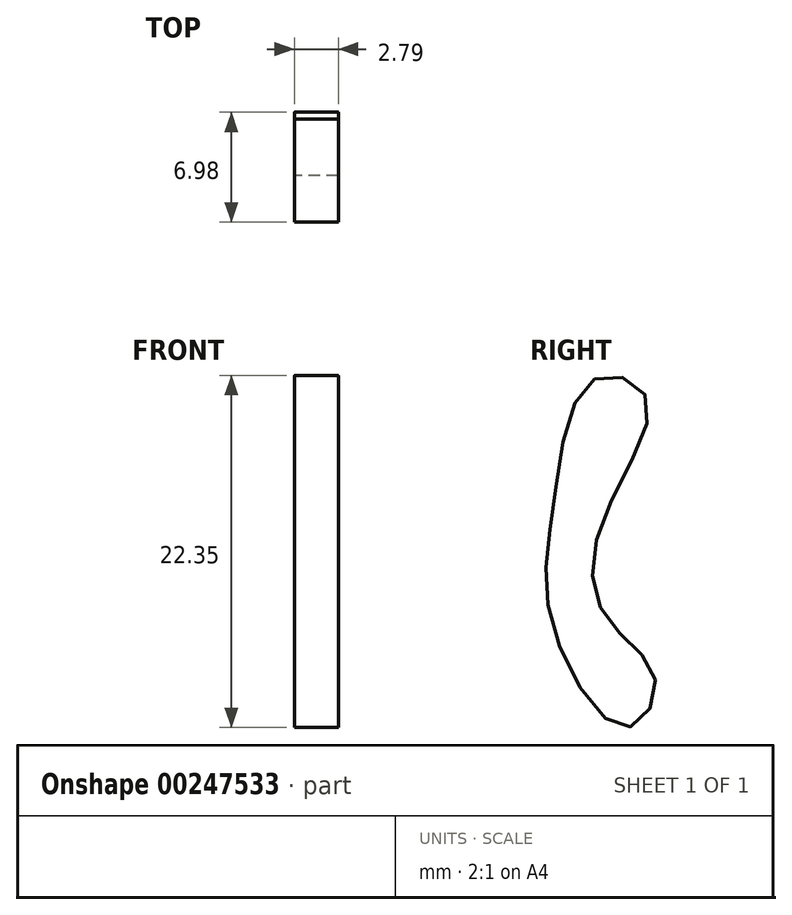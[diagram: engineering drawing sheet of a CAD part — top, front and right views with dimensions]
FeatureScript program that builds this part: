
annotation { "Feature Type Name" : "Feature", "Feature Type Description" : "" }
export const myFeature = defineFeature(function(context is Context, id is Id, definition is map)
    precondition{}
    {
        {
            var Q0;
            Q0=qCreatedBy(makeId("Right.planeOp"),FACE);
            var sketch = newSketch(context, id + "F0", { "sketchPlane" : qUnion([Q0])});
            skFitSpline(sketch, "E0", {"points": [v(-40.65, 39.62) * mm, v(-43.22, 31.9) * mm, v(-43.22, 23.67) * mm, v(-38.6, 17.5) * mm, v(-36.79, 20.58) * mm, v(-39.88, 24.44) * mm, v(-40.13, 30.61) * mm, v(-37.3, 38.33) * mm, v(-40.65, 39.62) * mm]});
            skSolve(sketch);
        }
        {
            var Q0;
            Q0 = qSketchRegion(id + "F0", true);
            extrude(context, id + "F1", {"entities" : qUnion([Q0]), "depth" : 2.8 * mm});
        }
    });
